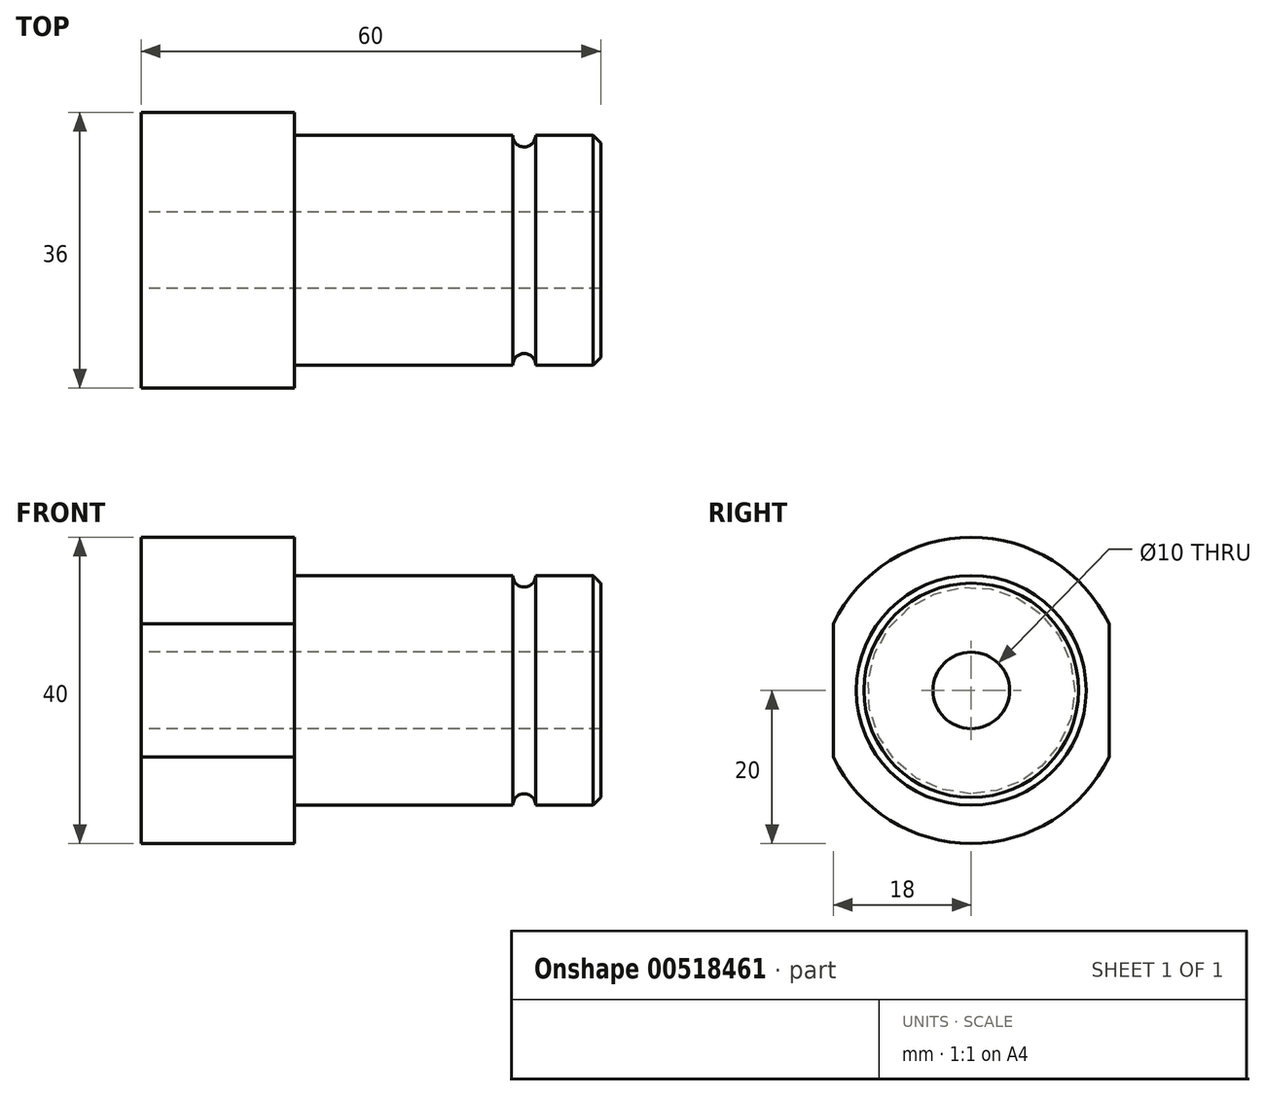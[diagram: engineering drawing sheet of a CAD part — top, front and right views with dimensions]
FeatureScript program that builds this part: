
annotation { "Feature Type Name" : "Feature", "Feature Type Description" : "" }
export const myFeature = defineFeature(function(context is Context, id is Id, definition is map)
    precondition{}
    {
        {
            var Q0;
            Q0=qCreatedBy(makeId("Front.planeOp"),FACE);
            var sketch = newSketch(context, id + "F0", { "sketchPlane" : qUnion([Q0])});
            skLineSegment(sketch, "E0", {"start": v(0, 0) * mm, "end": v(0, 20) * mm});
            skLineSegment(sketch, "E1", {"start": v(0, 20) * mm, "end": v(20, 20) * mm});
            skLineSegment(sketch, "E2", {"start": v(20, 20) * mm, "end": v(20, 15) * mm});
            skLineSegment(sketch, "E3", {"start": v(20, 15) * mm, "end": v(60, 15) * mm});
            skLineSegment(sketch, "E4", {"start": v(60, 15) * mm, "end": v(60, 0) * mm});
            skLineSegment(sketch, "E5", {"start": v(60, 0) * mm, "end": v(0, 0) * mm});
            skLineSegment(sketch, "E6", {"start": v(50, 15) * mm, "end": v(50, 0) * mm});
            skCircle(sketch, "E7", {"center": v(50, 15) * mm, "radius": 1.5 * mm});
            skSolve(sketch);
        }
        {
            var Q0;
            {var subQ6=sQuery(id+"F0.wireOp",EDGE,"E0");Q0=makeQuery(id+"F0.imprint","IMPRINT",FACE,{"disambiguationData":[TD([[makeQuery(id+"F0.imprint","IMPRINT",EDGE,{"derivedFrom":subQ6}),-1.0]])]});}
            var Q1;
            {var subQ1=sQuery(id+"F0.wireOp",EDGE,"E4");Q1=makeQuery(id+"F0.imprint","IMPRINT",FACE,{"disambiguationData":[TD([[makeQuery(id+"F0.imprint","IMPRINT",EDGE,{"derivedFrom":subQ1}),-1.0]])]});}
            var Q2;
            Q2=sQuery(id+"F0.wireOp",EDGE,"E5");
            revolve(context, id + "F1", {"entities" : qUnion([Q0, Q1]), "axis" : qUnion([Q2]), "revolveType" : RevolveType.FULL});
        }
        {
            var Q0;
            Q0=makeQuery(id+"F1.opRevolve","SWEPT_EDGE",EDGE,{"disambiguationData":[OSD([sQuery(id+"F0.wireOp",EDGE,"E3"),sQuery(id+"F0.wireOp",EDGE,"E4")])]});
            chamfer(context, id + "F2", {"entities" : qUnion([Q0]), "width" : 1 * mm, "tangentPropagation" : true});
        }
        {
            var Q0;
            Q0=makeQuery(id+"F1.opRevolve","SWEPT_FACE",FACE,{"disambiguationData":[OSD([sQuery(id+"F0.wireOp",EDGE,"E0")])]});
            var sketch = newSketch(context, id + "F3", { "sketchPlane" : qUnion([Q0])});
            skLineSegment(sketch, "E8", {"start": v(0, 24.73) * mm, "end": v(0, -28.06) * mm, "construction": true});
            skLineSegment(sketch, "E9", {"start": v(-18, 8.72) * mm, "end": v(-18, -8.72) * mm});
            skLineSegment(sketch, "E10.MirrorCS", {"start": v(18, 8.72) * mm, "end": v(18, -8.72) * mm});
            skSolve(sketch);
        }
        {
            var Q0;
            {var subQ0=sQuery(id+"F3.wireOp",EDGE,"E9");Q0=makeQuery(id+"F3.imprint","IMPRINT",FACE,{"disambiguationData":[TD([[makeQuery(id+"F3.imprint","IMPRINT",EDGE,{"derivedFrom":subQ0}),-1.0]])]});}
            var Q1;
            {var subQ0=sQuery(id+"F3.wireOp",EDGE,"E10.MirrorCS");Q1=makeQuery(id+"F3.imprint","IMPRINT",FACE,{"disambiguationData":[TD([[makeQuery(id+"F3.imprint","IMPRINT",EDGE,{"derivedFrom":subQ0}),1.0]])]});}
            extrude(context, id + "F4", {"entities" : qUnion([Q0, Q1]), "operationType" : NewBodyOperationType.REMOVE, "endBound" : BoundingType.UP_TO_NEXT, "oppositeDirection" : true, "depth" : 25 * mm, "offsetDistance" : 25 * mm});
        }
        {
            var Q0;
            Q0=makeQuery(id+"F1.opRevolve","SWEPT_FACE",FACE,{"disambiguationData":[OSD([sQuery(id+"F0.wireOp",EDGE,"E0")])]});
            var sketch = newSketch(context, id + "F5", { "sketchPlane" : qUnion([Q0])});
            skCircle(sketch, "E11", {"center": v(0, 0) * mm, "radius": 5 * mm});
            skSolve(sketch);
        }
        {
            var Q0;
            Q0 = qSketchRegion(id + "F5", true);
            extrude(context, id + "F6", {"entities" : qUnion([Q0]), "operationType" : NewBodyOperationType.REMOVE, "endBound" : BoundingType.UP_TO_NEXT, "oppositeDirection" : true, "depth" : 25 * mm, "offsetDistance" : 25 * mm});
        }
    });
